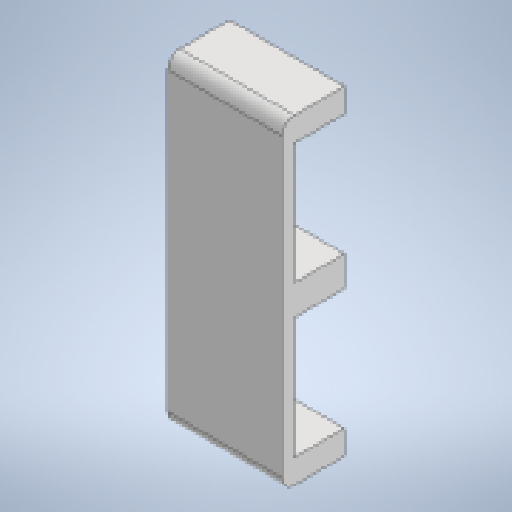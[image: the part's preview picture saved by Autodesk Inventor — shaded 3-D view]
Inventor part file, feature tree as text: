
AUTODESK INVENTOR PART (.ipt)
format: ipt  version: 2023 (Build 270158000, 158)  size: 244,224 bytes
history: native  units: in
note: dims shown in document units (in); Inventor stores cm internally (conversion verified against a paired STEP export)
features: reference x12, other x6, sketch x5, projected_geometry x5, extrude x4, fillet x2, hole x1
ambient origin geometry x8: Origin, YZ Plane, XZ Plane, XY Plane, X Axis, Y Axis, Z Axis, Center Point
bodies: Body1 (feature_tree)
feature tree (35):
  other  "Bryła1"
  sketch  "Szkic1"
  other  "Płaszczyzna konstrukcyjna1"
  extrude  "Wyciągnięcie proste1"  Depth=0.1575in
  extrude  "Wyciągnięcie proste2"  Depth=0.1575in
  hole  "Otwór1"  [1 undecoded]
  extrude  "Wyciągnięcie proste3"  Depth=0.0787in TaperAngle=0.0deg
  fillet  "Zaokrąglenie1"  Radius=0.0787in
  extrude  "Wyciągnięcie proste4"  Depth=0.0787in
  fillet  "Zaokrąglenie2"  Radius=0.0984in
  reference  "Odniesienie1"
  reference  "Odniesienie2"
  reference  "Odniesienie3"
  reference  "Odniesienie4"
  reference  "Odniesienie5"
  reference  "Odniesienie6"
  reference  "Odniesienie7"
  reference  "Odniesienie8"
  reference  "Odniesienie9"
  reference  "Odniesienie10"
  reference  "Odniesienie11"
  reference  "Odniesienie12"
  sketch  "Szkic2"
  projected_geometry  "Pętla rzutowana1"
  projected_geometry  "Pętla rzutowana2"
  projected_geometry  "Pętla rzutowana3"
  sketch  "Szkic3"
  sketch  "Szkic4"
  projected_geometry  "Pętla rzutowana4"
  sketch  "Szkic5"
  projected_geometry  "Pętla rzutowana5"
  other  "<userpath>\Desktop\MojeRoboty\Stefan\mechanics 2\STEFAN.iam"
  other  "STEFAN.iam"
  other  "servo_mini_1370hd_cos:1"
  other  "servo_mini_1370hd_cos:2"
note: 1 required parameter value undecoded (feature->parameter linkage not recoverable at this tier; creation-order binding heuristic only, values carry confidence <= 0.55)
